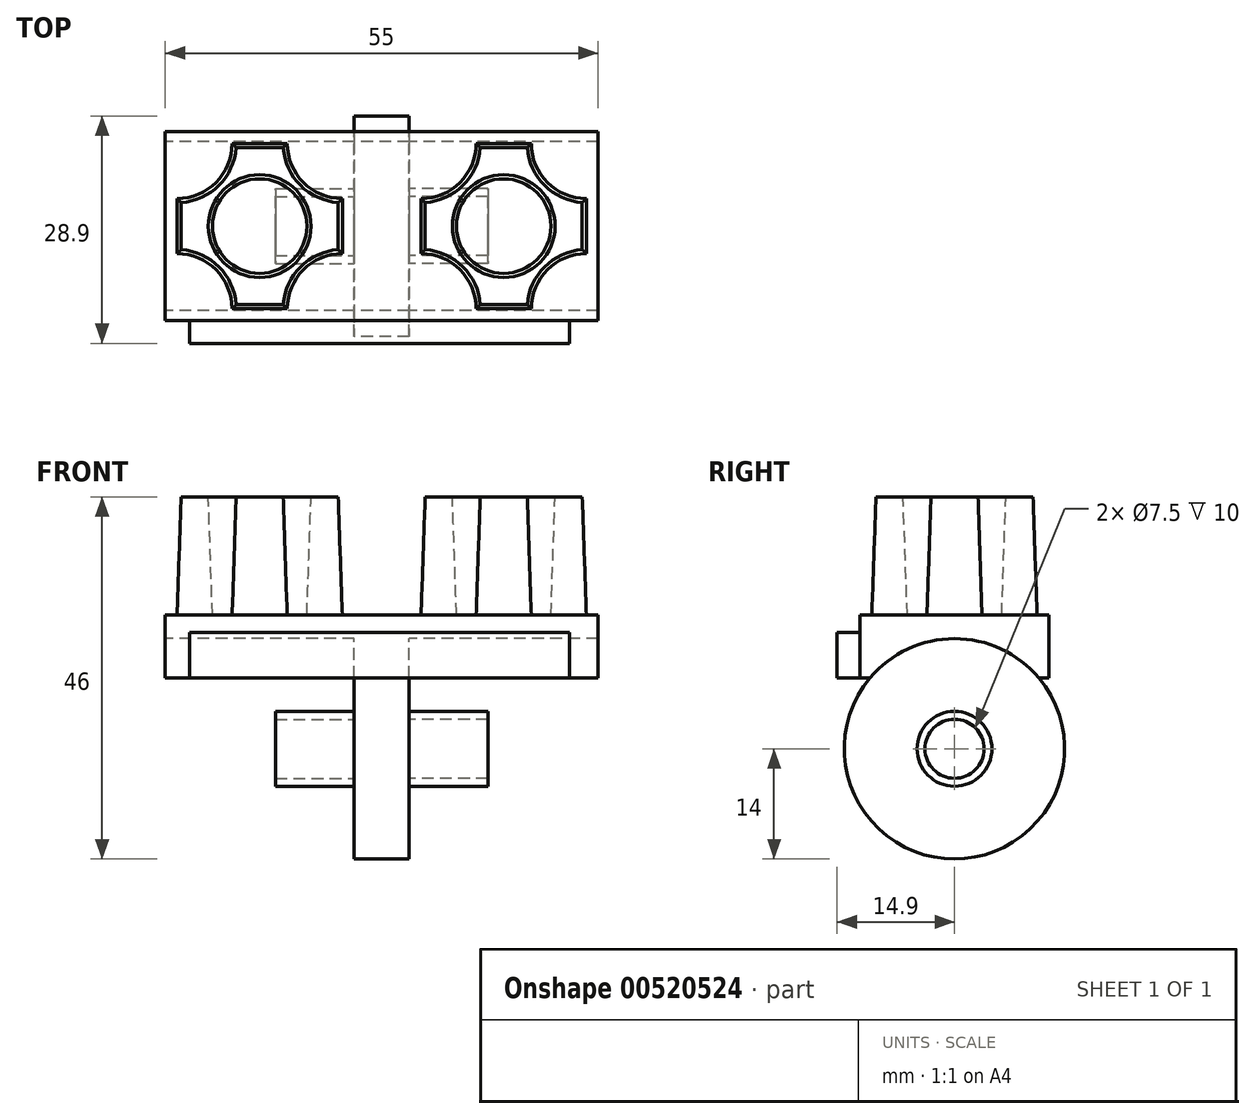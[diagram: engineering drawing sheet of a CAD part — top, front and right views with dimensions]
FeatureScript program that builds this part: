
annotation { "Feature Type Name" : "Feature", "Feature Type Description" : "" }
export const myFeature = defineFeature(function(context is Context, id is Id, definition is map)
    precondition{}
    {
        {
            var Q0;
            Q0=qCreatedBy(makeId("Top.planeOp"),FACE);
            var sketch = newSketch(context, id + "F0", { "sketchPlane" : qUnion([Q0])});
            skLineSegment(sketch, "E0.rect.bottom", {"start": v(-698.5, 300.46) * mm, "end": v(698.5, 300.46) * mm});
            skLineSegment(sketch, "E0.rect.top", {"start": v(-698.5, -300.46) * mm, "end": v(698.5, -300.46) * mm});
            skLineSegment(sketch, "E0.rect.left", {"start": v(-698.5, 300.46) * mm, "end": v(-698.5, -300.46) * mm});
            skLineSegment(sketch, "E0.rect.right", {"start": v(698.5, 300.46) * mm, "end": v(698.5, -300.46) * mm});
            skPoint(sketch, "E0.rect.middle", {"position": v(0, 0) * mm});
            skLineSegment(sketch, "E1.rect.bottom", {"start": v(-27.5, 12) * mm, "end": v(27.5, 12) * mm});
            skLineSegment(sketch, "E1.rect.top", {"start": v(-27.5, -12) * mm, "end": v(27.5, -12) * mm});
            skLineSegment(sketch, "E1.rect.left", {"start": v(-27.5, 12) * mm, "end": v(-27.5, -12) * mm});
            skLineSegment(sketch, "E1.rect.right", {"start": v(27.5, 12) * mm, "end": v(27.5, -12) * mm});
            skSolve(sketch);
        }
        {
            var Q0;
            Q0=makeQuery(id+"F0.imprint","IMPRINT",FACE,{"disambiguationData":[TD([[makeQuery(id+"F0.imprint","IMPRINT",EDGE,{"derivedFrom":sQuery(id+"F0.wireOp",EDGE,"E1.rect.bottom")}),-1.0]])]});
            extrude(context, id + "F1", {"entities" : qUnion([Q0]), "depth" : 8 * mm});
        }
        {
            var Q0;
            Q0=makeQuery(id+"F1.opExtrude","SWEPT_FACE",FACE,{"disambiguationData":[OSD([sQuery(id+"F0.wireOp",EDGE,"E1.rect.left")])]});
            var sketch = newSketch(context, id + "F2", { "sketchPlane" : qUnion([Q0])});
            skCircle(sketch, "E2", {"center": v(0, -9) * mm, "radius": 14 * mm});
            skSolve(sketch);
        }
        {
            var Q0;
            Q0=qSketchRegion(id+"F2",true);
            extrude(context, id + "F3", {"entities" : qUnion([Q0]), "operationType" : NewBodyOperationType.REMOVE, "oppositeDirection" : true, "depth" : 63.7 * mm});
        }
        {
            var Q0;
            Q0=qCreatedBy(makeId("Right.planeOp"),FACE);
            var sketch = newSketch(context, id + "F4", { "sketchPlane" : qUnion([Q0])});
            skCircle(sketch, "E3", {"center": v(0, -9) * mm, "radius": 14 * mm});
            skSolve(sketch);
        }
        {
            var Q0;
            Q0=makeQuery(id+"F4.imprint","IMPRINT",FACE,{"disambiguationData":[TD([[makeQuery(id+"F4.imprint","IMPRINT",EDGE,{"derivedFrom":sQuery(id+"F4.wireOp",EDGE,"E3")}),1.0]])]});
            extrude(context, id + "F5", {"entities" : qUnion([Q0]), "operationType" : NewBodyOperationType.ADD, "depth" : 3.5 * mm, "hasSecondDirection" : true, "secondDirectionOppositeDirection" : true, "secondDirectionDepth" : 3.5 * mm});
        }
        {
            var Q0;
            Q0=makeQuery(id+"F5.opExtrude","CAP_FACE",FACE,{"disambiguationData":[OSD([sQuery(id+"F4.wireOp",EDGE,"E3")])],"isStart":false});
            var sketch = newSketch(context, id + "F6", { "sketchPlane" : qUnion([Q0])});
            skCircle(sketch, "E4", {"center": v(0, -9) * mm, "radius": 3.75 * mm});
            skCircle(sketch, "E5", {"center": v(0, -9) * mm, "radius": 4.75 * mm});
            skSolve(sketch);
        }
        {
            var Q0;
            Q0=makeQuery(id+"F6.imprint","IMPRINT",FACE,{"disambiguationData":[TD([[makeQuery(id+"F6.imprint","IMPRINT",EDGE,{"derivedFrom":sQuery(id+"F6.wireOp",EDGE,"E4")}),-1.0]])]});
            extrude(context, id + "F7", {"entities" : qUnion([Q0]), "operationType" : NewBodyOperationType.ADD, "depth" : 10 * mm});
        }
        {
            var Q0;
            Q0=makeQuery(id+"F1.opExtrude","SWEPT_BODY",BODY,{"disambiguationData":[OSD([sQuery(id+"F0.wireOp",EDGE,"E1.rect.bottom"),sQuery(id+"F0.wireOp",EDGE,"E1.rect.top"),sQuery(id+"F0.wireOp",EDGE,"E1.rect.left"),sQuery(id+"F0.wireOp",EDGE,"E1.rect.right")])]});
            var Q1;
            Q1=qCreatedBy(makeId("Right.planeOp"),FACE);
            mirror(context, id + "F8", {"operationType" : NewBodyOperationType.ADD, "entities" : qUnion([Q0]), "mirrorPlane" : qUnion([Q1])});
        }
        {
            var Q0;
            Q0=makeQuery(id+"F1.opExtrude","CAP_FACE",FACE,{"disambiguationData":[OSD([sQuery(id+"F0.wireOp",EDGE,"E1.rect.bottom"),sQuery(id+"F0.wireOp",EDGE,"E1.rect.top"),sQuery(id+"F0.wireOp",EDGE,"E1.rect.left"),sQuery(id+"F0.wireOp",EDGE,"E1.rect.right")])],"isStart":false});
            var sketch = newSketch(context, id + "F9", { "sketchPlane" : qUnion([Q0])});
            skLineSegment(sketch, "E6.bottom", {"start": v(-19, 10.5) * mm, "end": v(-12, 10.5) * mm});
            skLineSegment(sketch, "E6.top", {"start": v(-19, -10.5) * mm, "end": v(-12, -10.5) * mm});
            skLineSegment(sketch, "E6.left", {"start": v(-26, 3.5) * mm, "end": v(-26, -3.5) * mm});
            skLineSegment(sketch, "E6.right", {"start": v(-5, 3.5) * mm, "end": v(-5, -3.5) * mm});
            skArc(sketch, "E7", {"start": v(-26, 3.5) * mm, "mid": v(-21.05, 5.55) * mm, "end": v(-19, 10.5) * mm});
            skArc(sketch, "E8", {"start": v(-12, 10.5) * mm, "mid": v(-9.95, 5.55) * mm, "end": v(-5, 3.5) * mm});
            skArc(sketch, "E9", {"start": v(-19, -10.5) * mm, "mid": v(-21.05, -5.55) * mm, "end": v(-26, -3.5) * mm});
            skArc(sketch, "E10", {"start": v(-5, -3.5) * mm, "mid": v(-9.95, -5.55) * mm, "end": v(-12, -10.5) * mm});
            skCircle(sketch, "E11", {"center": v(-15.5, 0) * mm, "radius": 6 * mm});
            skLineSegment(sketch, "E12", {"start": v(-15.5, 0) * mm, "end": v(-15.5, 10.5) * mm, "construction": true});
            skSolve(sketch);
        }
        {
            var Q0;
            Q0=makeQuery(id+"F9.imprint","IMPRINT",FACE,{"disambiguationData":[TD([[makeQuery(id+"F9.imprint","IMPRINT",EDGE,{"derivedFrom":sQuery(id+"F9.wireOp",EDGE,"E6.bottom")}),-1.0]])]});
            extrude(context, id + "F10", {"entities" : qUnion([Q0]), "operationType" : NewBodyOperationType.ADD, "depth" : 15 * mm, "hasDraft" : true, "draftAngle" : 2 * degree, "draftPullDirection" : true});
        }
        {
            var Q0;
            Q0=makeQuery(id+"F1.opExtrude","SWEPT_BODY",BODY,{"disambiguationData":[OSD([sQuery(id+"F0.wireOp",EDGE,"E1.rect.bottom"),sQuery(id+"F0.wireOp",EDGE,"E1.rect.top"),sQuery(id+"F0.wireOp",EDGE,"E1.rect.left"),sQuery(id+"F0.wireOp",EDGE,"E1.rect.right")])]});
            var Q1;
            Q1=qCreatedBy(makeId("Right.planeOp"),FACE);
            mirror(context, id + "F11", {"operationType" : NewBodyOperationType.ADD, "entities" : qUnion([Q0]), "mirrorPlane" : qUnion([Q1])});
        }
        {
            var Q0;
            Q0=qCreatedBy(makeId("Front.planeOp"),FACE);
            var sketch = newSketch(context, id + "F12", { "sketchPlane" : qUnion([Q0])});
            skLineSegment(sketch, "E13.bottom", {"start": v(-24.42, 0) * mm, "end": v(23.83, 0) * mm});
            skLineSegment(sketch, "E13.top", {"start": v(-24.42, 5.77) * mm, "end": v(23.83, 5.77) * mm});
            skLineSegment(sketch, "E13.left", {"start": v(-24.42, 0) * mm, "end": v(-24.42, 5.77) * mm});
            skLineSegment(sketch, "E13.right", {"start": v(23.83, 0) * mm, "end": v(23.83, 5.77) * mm});
            skSolve(sketch);
        }
        {
            var Q0;
            Q0 = qSketchRegion(id + "F12", true);
            extrude(context, id + "F13", {"entities" : qUnion([Q0]), "operationType" : NewBodyOperationType.ADD, "depth" : 14.9 * mm, "offsetDistance" : 25 * mm, "hasSecondDirection" : true, "secondDirectionOppositeDirection" : false, "secondDirectionDepth" : 11.1 * mm});
        }
    });
